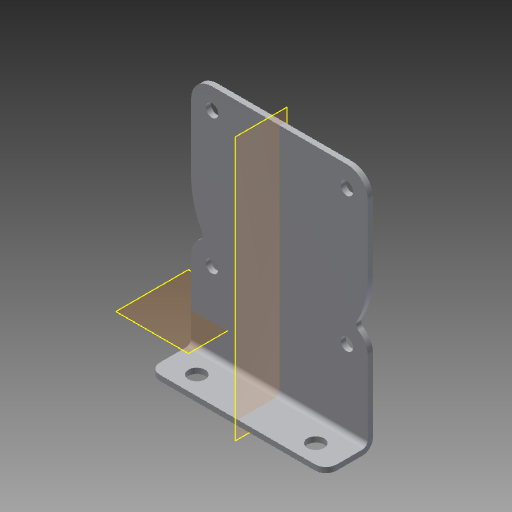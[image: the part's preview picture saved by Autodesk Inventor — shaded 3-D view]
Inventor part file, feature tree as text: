
AUTODESK INVENTOR PART (.ipt)
format: ipt  version: 2017.1 (Build 211199000, 199)  size: 186,880 bytes
history: native  units: in
note: dims shown in document units (in); Inventor stores cm internally (conversion verified against a paired STEP export)
features: sketch x6, extrude x4, fillet x3, hole x2, reference x2, plane x1, mirror x1
ambient origin geometry x8: Origin, YZ Plane, XZ Plane, XY Plane, X Axis, Y Axis, Z Axis, Center Point
bodies: Solid1 (feature_tree)
feature tree (19):
  extrude  "Extrusion1"  Depth=2.11in
  extrude  "Extrusion5"  Depth=2.11in
  extrude  "Extrusion2"  Depth=0.5in TaperAngle=0.0deg
  extrude  "Extrusion4"  Depth=0.25in TaperAngle=0.0deg
  hole  "Hole3"  [1 undecoded]
  plane  "Work Plane1"
  fillet  "Fillet3"  Radius=0.063in
  fillet  "Fillet4"  Radius=0.125in
  fillet  "Fillet5"  Radius=0.125in
  hole  "Hole6"  [1 undecoded]
  mirror  "Mirror1"
  sketch  "Sketch1"  dims[d0=2.11in d1=2.5in]
  sketch  "Sketch2"  dims[d2=0.0625in d3=0.0in d4=2.11in]
  sketch  "Sketch6"  dims[d6=0.5in d7=0.0in d29=1.0in d30=0.0in]
  reference  "Reference2"
  sketch  "Sketch7"  dims[d31=0.15in d32=0.75in d33=0.279in d34=0.25in d35=0.5635in d36=1.0in d37=0.8108in d57=1.0in d58=0.0in]
  sketch  "Sketch9"  dims[d59=0.063in d60=2.856in d61=0.063in d62=0.125in d63=0.125in]
  sketch  "Sketch10"  dims[d64=0.201in d65=0.75in d66=0.385in d67=0.25in d68=0.5635in d69=1.0in d70=0.8108in]
  reference  "Reference3"
note: 2 required parameter values undecoded (feature->parameter linkage not recoverable at this tier; creation-order binding heuristic only, values carry confidence <= 0.55)
